# Revit family: ARX09-main
name_source: partatom
category: Lighting Fixtures
revit_build: Autodesk Revit MEP 2012 (Build: 20110309_2315(x64)
units: mm (PartAtom-declared; Revit-internal decimal feet)

## types (6) — shared parameters
Apparent Load = 0 VA
Connector Description = Lighting Connector
Default Elevation = 4' - 0"
Description = ArcheType X Site/Area
Glass = Hubbell - Glass
Height = 10' - 0"
Lamp = 54 LED Lamp
Load Classification = Lighting
Manufacturer = Kim Lighting
Manufacturer Fax = (626)-369-2695
Model = ARX09
Photometry = http://www.kimlighting.com
Product Documentation Link = http://cdn.kimlighting.com
Product Page URL = http://www.kimlighting.com
URL = http://www.kimlighting.com
Voltage = 120 V

## per-type parameters (varying)
| type | Finish |
| Black | Hubbell - Black |
| Dark Bronze | Hubbell - Dark Bronze |
| Light Gray | Hubbell - Light Gray |
| Platinum Silver | Hubbell - Platinum Silver |
| Titanium | Hubbell - Titanium |
| White | Hubbell - White |

## geometry (parser evidence)
native form markers: Blend x2, Sweep x7
no freeform markers — native parametric forms only
